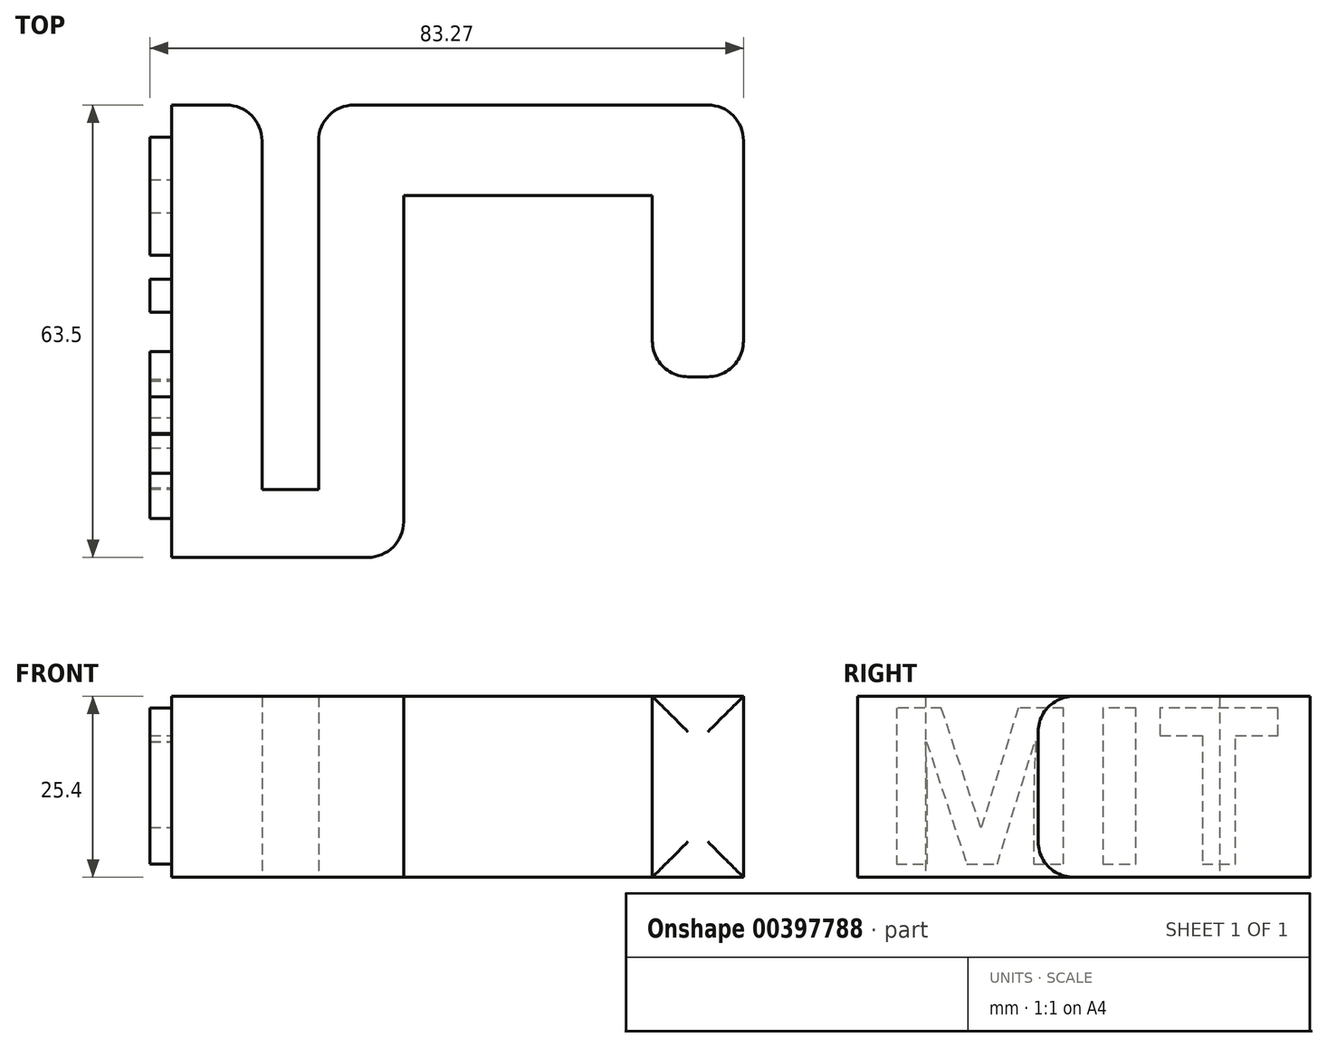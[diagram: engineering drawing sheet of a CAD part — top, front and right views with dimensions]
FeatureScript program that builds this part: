
annotation { "Feature Type Name" : "Feature", "Feature Type Description" : "" }
export const myFeature = defineFeature(function(context is Context, id is Id, definition is map)
    precondition{}
    {
        {
            var Q0;
            Q0=qCreatedBy(makeId("Top.planeOp"),FACE);
            var sketch = newSketch(context, id + "F0", { "sketchPlane" : qUnion([Q0])});
            skLineSegment(sketch, "E0", {"start": v(0, 0) * mm, "end": v(0, 63.5) * mm});
            skLineSegment(sketch, "E1", {"start": v(0, 63.5) * mm, "end": v(12.7, 63.5) * mm});
            skLineSegment(sketch, "E2", {"start": v(12.7, 63.5) * mm, "end": v(12.7, 9.53) * mm});
            skLineSegment(sketch, "E3", {"start": v(12.7, 9.53) * mm, "end": v(20.64, 9.53) * mm});
            skLineSegment(sketch, "E4", {"start": v(20.64, 9.53) * mm, "end": v(20.64, 63.5) * mm});
            skLineSegment(sketch, "E5", {"start": v(20.64, 63.5) * mm, "end": v(80.27, 63.5) * mm});
            skLineSegment(sketch, "E6", {"start": v(80.27, 63.5) * mm, "end": v(80.27, 25.35) * mm});
            skLineSegment(sketch, "E7", {"start": v(80.27, 25.35) * mm, "end": v(67.48, 25.35) * mm});
            skLineSegment(sketch, "E8", {"start": v(67.48, 25.35) * mm, "end": v(67.48, 50.8) * mm});
            skLineSegment(sketch, "E9", {"start": v(67.48, 50.8) * mm, "end": v(32.58, 50.8) * mm});
            skLineSegment(sketch, "E10", {"start": v(32.58, 50.8) * mm, "end": v(32.58, 0) * mm});
            skLineSegment(sketch, "E11", {"start": v(32.58, 0) * mm, "end": v(0, 0) * mm});
            skSolve(sketch);
        }
        {
            var Q0;
            Q0=makeQuery(id+"F0.imprint","IMPRINT",FACE,{"disambiguationData":[TD([[makeQuery(id+"F0.imprint","IMPRINT",EDGE,{"derivedFrom":sQuery(id+"F0.wireOp",EDGE,"E0")}),-1.0]])]});
            extrude(context, id + "F1", {"entities" : qUnion([Q0]), "depth" : 25.4 * mm});
        }
        {
            var Q0;
            Q0=makeQuery(id+"F1.opExtrude","SWEPT_FACE",FACE,{"disambiguationData":[OSD([sQuery(id+"F0.wireOp",EDGE,"E0")])]});
            var sketch = newSketch(context, id + "F2", { "sketchPlane" : qUnion([Q0])});
            skText(sketch, "E12", { "text": "TIM", "fontName": "OpenSans-Bold.ttf"});
            const initialGuessF2  = {"E12": [-0.05962, 0.00183, 1, 0, 0.02212]};
            skSetInitialGuess(sketch, initialGuessF2);
            skSolve(sketch);
        }
        {
            var Q0;
            Q0=qSketchRegion(id+"F2",true);
            extrude(context, id + "F3", {"entities" : qUnion([Q0]), "operationType" : NewBodyOperationType.ADD, "depth" : 3 * mm});
        }
        {
            var Q0;
            Q0=makeQuery(id+"F1.opExtrude","CAP_EDGE",EDGE,{"disambiguationData":[OSD([sQuery(id+"F0.wireOp",EDGE,"E7")])],"isStart":false});
            var Q1;
            Q1=makeQuery(id+"F1.opExtrude","CAP_EDGE",EDGE,{"disambiguationData":[OSD([sQuery(id+"F0.wireOp",EDGE,"E7")])],"isStart":true});
            var Q2;
            Q2=makeQuery(id+"F1.opExtrude","SWEPT_EDGE",EDGE,{"disambiguationData":[OSD([sQuery(id+"F0.wireOp",EDGE,"E6"),sQuery(id+"F0.wireOp",EDGE,"E7")])]});
            var Q3;
            Q3=makeQuery(id+"F1.opExtrude","SWEPT_EDGE",EDGE,{"disambiguationData":[OSD([sQuery(id+"F0.wireOp",EDGE,"E7"),sQuery(id+"F0.wireOp",EDGE,"E8")])]});
            var Q4;
            Q4=makeQuery(id+"F1.opExtrude","SWEPT_EDGE",EDGE,{"disambiguationData":[OSD([sQuery(id+"F0.wireOp",EDGE,"E5"),sQuery(id+"F0.wireOp",EDGE,"E6")])]});
            var Q5;
            Q5=makeQuery(id+"F1.opExtrude","SWEPT_EDGE",EDGE,{"disambiguationData":[OSD([sQuery(id+"F0.wireOp",EDGE,"E10"),sQuery(id+"F0.wireOp",EDGE,"E11")])]});
            var Q6;
            Q6=makeQuery(id+"F1.opExtrude","SWEPT_EDGE",EDGE,{"disambiguationData":[OSD([sQuery(id+"F0.wireOp",EDGE,"E4"),sQuery(id+"F0.wireOp",EDGE,"E5")])]});
            var Q7;
            Q7=makeQuery(id+"F1.opExtrude","SWEPT_EDGE",EDGE,{"disambiguationData":[OSD([sQuery(id+"F0.wireOp",EDGE,"E1"),sQuery(id+"F0.wireOp",EDGE,"E2")])]});
            fillet(context, id + "F4", {"entities" : qUnion([Q0, Q1, Q2, Q3, Q4, Q5, Q6, Q7]), "radius" : 5 * mm, "tangentPropagation" : true, "allowEdgeOverflow" : false});
        }
    });
